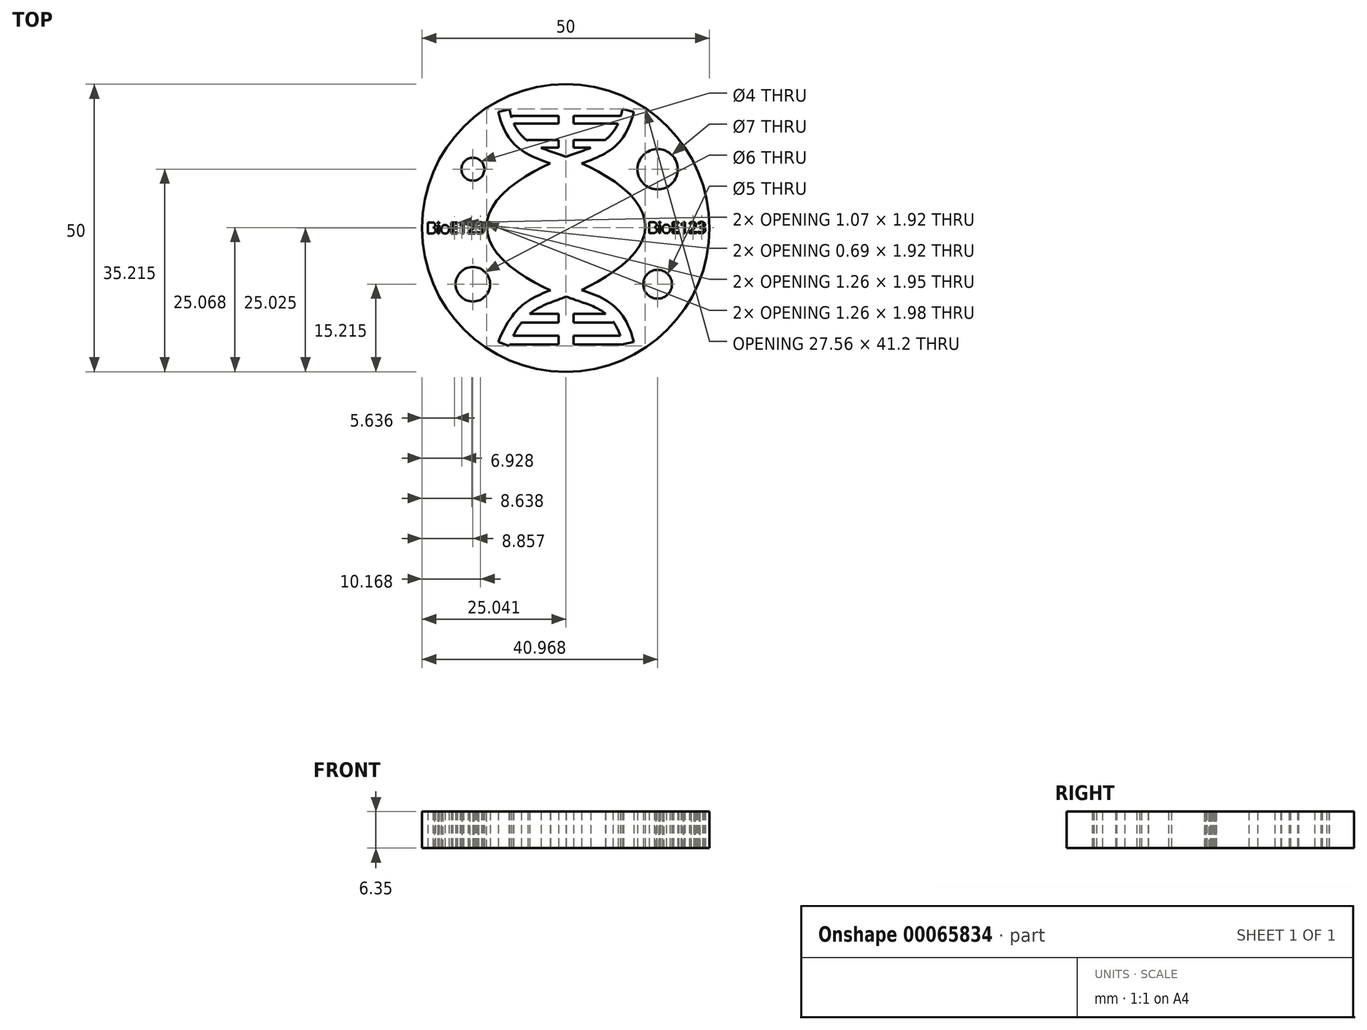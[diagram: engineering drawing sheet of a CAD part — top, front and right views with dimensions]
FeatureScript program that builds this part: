
annotation { "Feature Type Name" : "Feature", "Feature Type Description" : "" }
export const myFeature = defineFeature(function(context is Context, id is Id, definition is map)
    precondition{}
    {
        {
            var Q0;
            Q0=qCreatedBy(makeId("Top.planeOp"),FACE);
            var sketch = newSketch(context, id + "F0", { "sketchPlane" : qUnion([Q0])});
            skFitSpline(sketch, "E0", {"points": [v(-11.73, 20.22) * mm, v(0.04, 10.22) * mm, v(11.81, 0.22) * mm, v(0.04, -9.78) * mm, v(-11.73, -19.78) * mm], "startDerivative": vector(19.4, -88.4) * mm, "endDerivative": vector(-36.7, -91) * mm});
            skFitSpline(sketch, "E1", {"points": [v(11.81, 20.22) * mm, v(0.04, 10.22) * mm, v(-11.73, 0.22) * mm, v(0.04, -9.78) * mm, v(11.81, -19.78) * mm], "startDerivative": vector(-20.61, -88.4) * mm, "endDerivative": vector(22.4, -91) * mm});
            skPoint(sketch, "E2.endSnap0", {"position": v(5.3, 0.24) * mm});
            skCircle(sketch, "E3", {"center": v(-16.14, 10.22) * mm, "radius": 2 * mm});
            skCircle(sketch, "E4", {"center": v(15.97, 10.22) * mm, "radius": 3.5 * mm});
            skCircle(sketch, "E5", {"center": v(-16.14, -9.78) * mm, "radius": 3 * mm});
            skCircle(sketch, "E6", {"center": v(15.97, -9.78) * mm, "radius": 2.5 * mm});
            skLineSegment(sketch, "E7.bottom", {"start": v(-8.24, -14.9) * mm, "end": v(-1.23, -14.9) * mm});
            skLineSegment(sketch, "E7.top", {"start": v(-8.24, -16.48) * mm, "end": v(-1.23, -16.48) * mm});
            skLineSegment(sketch, "E7.left", {"start": v(-8.24, -14.9) * mm, "end": v(-8.24, -16.48) * mm});
            skLineSegment(sketch, "E7.right", {"start": v(-1.23, -14.9) * mm, "end": v(-1.23, -16.48) * mm});
            skLineSegment(sketch, "E8.bottom", {"start": v(8.24, -14.9) * mm, "end": v(1.35, -14.9) * mm});
            skLineSegment(sketch, "E8.top", {"start": v(8.24, -16.48) * mm, "end": v(1.35, -16.48) * mm});
            skLineSegment(sketch, "E8.left", {"start": v(8.24, -14.9) * mm, "end": v(8.24, -16.48) * mm});
            skLineSegment(sketch, "E8.right", {"start": v(1.35, -14.9) * mm, "end": v(1.35, -16.48) * mm});
            skLineSegment(sketch, "E9.bottom", {"start": v(-9.9, -18.72) * mm, "end": v(-1.23, -18.72) * mm});
            skLineSegment(sketch, "E9.top", {"start": v(-9.9, -20.23) * mm, "end": v(-1.23, -20.23) * mm});
            skLineSegment(sketch, "E9.left", {"start": v(-9.9, -18.72) * mm, "end": v(-9.9, -20.23) * mm});
            skLineSegment(sketch, "E9.right", {"start": v(-1.23, -18.72) * mm, "end": v(-1.23, -20.23) * mm});
            skLineSegment(sketch, "E10.bottom", {"start": v(10.03, -18.72) * mm, "end": v(1.35, -18.72) * mm});
            skLineSegment(sketch, "E10.top", {"start": v(10.03, -20.23) * mm, "end": v(1.35, -20.23) * mm});
            skLineSegment(sketch, "E10.left", {"start": v(10.03, -18.72) * mm, "end": v(10.03, -20.23) * mm});
            skLineSegment(sketch, "E10.right", {"start": v(1.35, -18.72) * mm, "end": v(1.35, -20.23) * mm});
            skLineSegment(sketch, "E11", {"start": v(9.87, -20.26) * mm, "end": v(11.81, -19.78) * mm});
            skLineSegment(sketch, "E12", {"start": v(-9.87, -20.53) * mm, "end": v(-11.73, -19.78) * mm});
            skLineSegment(sketch, "E13", {"start": v(-11.73, 20.22) * mm, "end": v(-9.78, 20.64) * mm});
            skLineSegment(sketch, "E14", {"start": v(11.81, 20.22) * mm, "end": v(9.86, 20.67) * mm});
            skLineSegment(sketch, "E15.bottom", {"start": v(-6.6, 13.94) * mm, "end": v(-1.23, 13.94) * mm});
            skLineSegment(sketch, "E15.top", {"start": v(-6.6, 15.33) * mm, "end": v(-1.23, 15.33) * mm});
            skLineSegment(sketch, "E15.left", {"start": v(-6.6, 13.94) * mm, "end": v(-6.6, 15.33) * mm});
            skLineSegment(sketch, "E15.right", {"start": v(-1.23, 13.94) * mm, "end": v(-1.23, 15.33) * mm});
            skLineSegment(sketch, "E16.bottom", {"start": v(7.26, 13.94) * mm, "end": v(1.35, 13.94) * mm});
            skLineSegment(sketch, "E16.top", {"start": v(7.26, 15.33) * mm, "end": v(1.35, 15.33) * mm});
            skLineSegment(sketch, "E16.left", {"start": v(7.26, 13.94) * mm, "end": v(7.26, 15.33) * mm});
            skLineSegment(sketch, "E16.right", {"start": v(1.35, 13.94) * mm, "end": v(1.35, 15.33) * mm});
            skLineSegment(sketch, "E17.bottom", {"start": v(-9.43, 18.17) * mm, "end": v(-1.23, 18.17) * mm});
            skLineSegment(sketch, "E17.top", {"start": v(-9.43, 19.5) * mm, "end": v(-1.23, 19.5) * mm});
            skLineSegment(sketch, "E17.left", {"start": v(-9.43, 18.17) * mm, "end": v(-9.43, 19.5) * mm});
            skLineSegment(sketch, "E17.right", {"start": v(-1.23, 18.17) * mm, "end": v(-1.23, 19.5) * mm});
            skLineSegment(sketch, "E18.bottom", {"start": v(9.87, 18.17) * mm, "end": v(1.35, 18.17) * mm});
            skLineSegment(sketch, "E18.top", {"start": v(9.87, 19.5) * mm, "end": v(1.35, 19.5) * mm});
            skLineSegment(sketch, "E18.left", {"start": v(9.87, 18.17) * mm, "end": v(9.87, 19.5) * mm});
            skLineSegment(sketch, "E18.right", {"start": v(1.35, 18.17) * mm, "end": v(1.35, 19.5) * mm});
            skText(sketch, "E19", { "text": "JD", "fontName": "OpenSans-Regular.ttf"});
            skFitSpline(sketch, "E20.0", {"points": [v(-9.78, 20.64) * mm, v(-9.6, 19.82) * mm, v(-9.16, 18.41) * mm, v(-8.34, 16.9) * mm, v(-7.4, 15.8) * mm, v(-6.27, 14.93) * mm, v(-4.88, 14.2) * mm, v(-3.23, 13.53) * mm, v(-1.65, 12.98) * mm, v(-0.3, 12.49) * mm, v(0.77, 12.08) * mm, v(1.87, 11.63) * mm, v(3.34, 10.98) * mm, v(5.17, 10.07) * mm, v(7.3, 8.84) * mm, v(9.28, 7.48) * mm, v(11.04, 5.98) * mm, v(12.25, 4.6) * mm, v(13.02, 3.37) * mm, v(13.47, 2.37) * mm, v(13.71, 1.48) * mm, v(13.8, 0.73) * mm, v(13.82, 0.16) * mm, v(13.78, -0.4) * mm, v(13.64, -1.15) * mm, v(13.36, -2.02) * mm, v(12.87, -3) * mm, v(12.06, -4.2) * mm, v(10.82, -5.58) * mm, v(9.04, -7.07) * mm, v(7.07, -8.43) * mm, v(4.98, -9.66) * mm, v(3.21, -10.56) * mm, v(1.82, -11.2) * mm, v(0.8, -11.64) * mm, v(-0.18, -12.03) * mm, v(-1.4, -12.5) * mm, v(-2.8, -13.03) * mm, v(-4.26, -13.66) * mm, v(-5.52, -14.37) * mm, v(-6.64, -15.25) * mm, v(-7.72, -16.44) * mm, v(-8.8, -18.12) * mm, v(-9.52, -19.65) * mm, v(-9.87, -20.53) * mm]});
            skFitSpline(sketch, "E21.0", {"points": [v(-9.78, 20.64) * mm, v(-9.6, 19.82) * mm, v(-9.16, 18.41) * mm, v(-8.34, 16.9) * mm, v(-7.4, 15.8) * mm, v(-6.27, 14.93) * mm, v(-4.88, 14.2) * mm, v(-3.23, 13.53) * mm, v(-1.65, 12.98) * mm, v(-0.3, 12.49) * mm, v(0.77, 12.08) * mm, v(1.87, 11.63) * mm, v(3.34, 10.98) * mm, v(5.17, 10.07) * mm, v(7.3, 8.84) * mm, v(9.28, 7.48) * mm, v(11.04, 5.98) * mm, v(12.25, 4.6) * mm, v(13.02, 3.37) * mm, v(13.47, 2.37) * mm, v(13.71, 1.48) * mm, v(13.8, 0.73) * mm, v(13.82, 0.16) * mm, v(13.78, -0.4) * mm, v(13.64, -1.15) * mm, v(13.36, -2.02) * mm, v(12.87, -3) * mm, v(12.06, -4.2) * mm, v(10.82, -5.58) * mm, v(9.04, -7.07) * mm, v(7.07, -8.43) * mm, v(4.98, -9.66) * mm, v(3.21, -10.56) * mm, v(1.82, -11.2) * mm, v(0.8, -11.64) * mm, v(-0.18, -12.03) * mm, v(-1.4, -12.5) * mm, v(-2.8, -13.03) * mm, v(-4.26, -13.66) * mm, v(-5.52, -14.37) * mm, v(-6.64, -15.25) * mm, v(-7.72, -16.44) * mm, v(-8.8, -18.12) * mm, v(-9.52, -19.65) * mm, v(-9.87, -20.53) * mm]});
            skFitSpline(sketch, "E22.0", {"points": [v(9.86, 20.67) * mm, v(9.67, 19.84) * mm, v(9.21, 18.43) * mm, v(8.38, 16.9) * mm, v(7.43, 15.8) * mm, v(6.3, 14.93) * mm, v(4.91, 14.2) * mm, v(3.27, 13.53) * mm, v(1.7, 12.98) * mm, v(0.36, 12.48) * mm, v(-0.7, 12.08) * mm, v(-1.78, 11.63) * mm, v(-3.24, 10.98) * mm, v(-5.06, 10.07) * mm, v(-7.18, 8.84) * mm, v(-9.15, 7.48) * mm, v(-10.9, 5.98) * mm, v(-12.11, 4.6) * mm, v(-12.89, 3.38) * mm, v(-13.35, 2.4) * mm, v(-13.6, 1.52) * mm, v(-13.71, 0.78) * mm, v(-13.74, 0.2) * mm, v(-13.7, -0.36) * mm, v(-13.6, -1.1) * mm, v(-13.34, -1.98) * mm, v(-12.87, -2.96) * mm, v(-12.1, -4.18) * mm, v(-10.88, -5.57) * mm, v(-9.13, -7.07) * mm, v(-7.16, -8.43) * mm, v(-5.04, -9.66) * mm, v(-3.22, -10.57) * mm, v(-1.77, -11.21) * mm, v(-0.68, -11.65) * mm, v(0.37, -12.05) * mm, v(1.7, -12.52) * mm, v(3.25, -13.05) * mm, v(4.87, -13.7) * mm, v(6.23, -14.4) * mm, v(7.35, -15.26) * mm, v(8.31, -16.37) * mm, v(9.17, -17.94) * mm, v(9.66, -19.4) * mm, v(9.87, -20.26) * mm]});
            skFitSpline(sketch, "E23.0", {"points": [v(9.86, 20.67) * mm, v(9.67, 19.84) * mm, v(9.21, 18.43) * mm, v(8.38, 16.9) * mm, v(7.43, 15.8) * mm, v(6.3, 14.93) * mm, v(4.91, 14.2) * mm, v(3.27, 13.53) * mm, v(1.7, 12.98) * mm, v(0.36, 12.48) * mm, v(-0.7, 12.08) * mm, v(-1.78, 11.63) * mm, v(-3.24, 10.98) * mm, v(-5.06, 10.07) * mm, v(-7.18, 8.84) * mm, v(-9.15, 7.48) * mm, v(-10.9, 5.98) * mm, v(-12.11, 4.6) * mm, v(-12.89, 3.38) * mm, v(-13.35, 2.4) * mm, v(-13.6, 1.52) * mm, v(-13.71, 0.78) * mm, v(-13.74, 0.2) * mm, v(-13.7, -0.36) * mm, v(-13.6, -1.1) * mm, v(-13.34, -1.98) * mm, v(-12.87, -2.96) * mm, v(-12.1, -4.18) * mm, v(-10.88, -5.57) * mm, v(-9.13, -7.07) * mm, v(-7.16, -8.43) * mm, v(-5.04, -9.66) * mm, v(-3.22, -10.57) * mm, v(-1.77, -11.21) * mm, v(-0.68, -11.65) * mm, v(0.37, -12.05) * mm, v(1.7, -12.52) * mm, v(3.25, -13.05) * mm, v(4.87, -13.7) * mm, v(6.23, -14.4) * mm, v(7.35, -15.26) * mm, v(8.31, -16.37) * mm, v(9.17, -17.94) * mm, v(9.66, -19.4) * mm, v(9.87, -20.26) * mm]});
            skLineSegment(sketch, "E24", {"start": v(11.7, 1.22) * mm, "end": v(13.64, 1.69) * mm});
            skLineSegment(sketch, "E25", {"start": v(11.65, -0.78) * mm, "end": v(13.57, -1.33) * mm});
            skLineSegment(sketch, "E26", {"start": v(-13.52, 1.78) * mm, "end": v(-11.59, 1.26) * mm});
            skLineSegment(sketch, "E27", {"start": v(-11.61, -0.7) * mm, "end": v(-13.56, -1.18) * mm});
            skCircle(sketch, "E28", {"center": v(0, 0) * mm, "radius": 25 * mm});
            skText(sketch, "E29", { "text": "BioE123", "fontName": "OpenSans-Regular.ttf"});
            skText(sketch, "E30", { "text": "BioE123", "fontName": "OpenSans-Regular.ttf"});
            const initialGuessF0  = {"E19": [-0.00498, -0.0039, 1, 0, 0.00933], "E29": [-0.02422, -0.00095, 1, 0, 0.00194], "E30": [0.01424, -0.00089, 1, 0, 0.00194]};
            skSetInitialGuess(sketch, initialGuessF0);
            skSolve(sketch);
        }
        {
            var Q0;
            Q0 = qSketchRegion(id + "F0", true);
            extrude(context, id + "F1", {"entities" : qUnion([Q0]), "depth" : 6.35 * mm});
        }
    });
